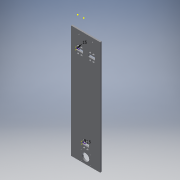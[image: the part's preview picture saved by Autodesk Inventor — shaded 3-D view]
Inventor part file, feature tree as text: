
AUTODESK INVENTOR PART (.ipt)
format: ipt  version: 2019 (Build 230136000, 136)  size: 220,672 bytes
history: native  units: in
note: dims shown in document units (in); Inventor stores cm internally (conversion verified against a paired STEP export)
features: reference x6, other x4, sketch x3, extrude x1
ambient origin geometry x8: Origin, YZ Plane, XZ Plane, XY Plane, X Axis, Y Axis, Z Axis, Center Point
bodies: Solid1 (feature_tree)
feature tree (14):
  extrude  "Extrusion1"  Depth=0.3465in
  sketch  "Sketch2"  dims[d3=3.937in]
  sketch  "Sketch3"  dims[d4=0.1969in d5=0.0in d6=0.5906in d8=0.5906in d9=2.1654in d10=2.1654in d11=0.128in d12=1.2205in d13=0.1969in d14=0.9843in d15=0.1575in d16=0.315in d17=0.1969in d18=0.0984in d19=0.1673in d20=0.1673in d21=1.8504in d22=0.4724in d23=0.1673in d24=0.1673in d25=1.063in d26=0.2756in d27=0.1673in d28=0.1673in]
  sketch  "Sketch1"  dims[d1=0.9449in d2=0.3465in]
  reference  "Reference1"
  reference  "Reference2"
  reference  "Reference3"
  reference  "Reference4"
  reference  "Reference5"
  reference  "Reference6"
  other  "<userpath>\Stuff\TPINFO\tp-info\XCart.iam"
  other  "XCart.iam"
  other  "YPulleySupport:1"
  other  "YPulleySupportBase:1"
